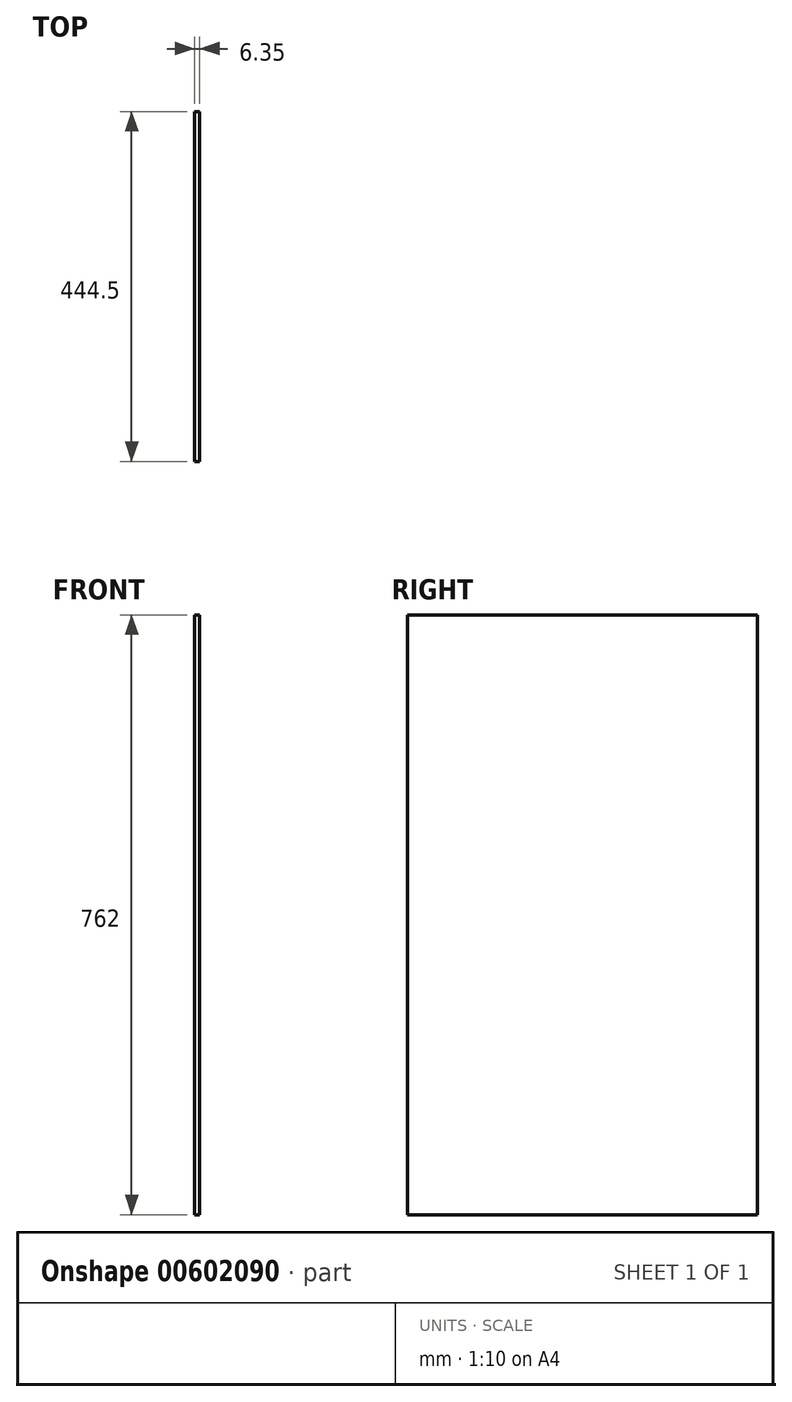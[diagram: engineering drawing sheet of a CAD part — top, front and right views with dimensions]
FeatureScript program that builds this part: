
annotation { "Feature Type Name" : "Feature", "Feature Type Description" : "" }
export const myFeature = defineFeature(function(context is Context, id is Id, definition is map)
    precondition{}
    {
        {
            var Q0;
            Q0=qCreatedBy(makeId("Right.planeOp"),FACE);
            var sketch = newSketch(context, id + "F0", { "sketchPlane" : qUnion([Q0])});
            skLineSegment(sketch, "E0.bottom", {"start": v(222.25, 381) * mm, "end": v(-222.25, 381) * mm});
            skLineSegment(sketch, "E0.top", {"start": v(222.25, -381) * mm, "end": v(-222.25, -381) * mm});
            skLineSegment(sketch, "E0.left", {"start": v(222.25, 381) * mm, "end": v(222.25, -381) * mm});
            skLineSegment(sketch, "E0.right", {"start": v(-222.25, 381) * mm, "end": v(-222.25, -381) * mm});
            skPoint(sketch, "E0.middle", {"position": v(0, 0) * mm});
            skSolve(sketch);
        }
        {
            var Q0;
            Q0=makeQuery(id+"F0.imprint","IMPRINT",FACE,{"disambiguationData":[TD([[makeQuery(id+"F0.imprint","IMPRINT",EDGE,{"derivedFrom":sQuery(id+"F0.wireOp",EDGE,"E0.bottom")}),1.0]])]});
            extrude(context, id + "F1", {"entities" : qUnion([Q0]), "depth" : 6.35 * mm, "offsetDistance" : 25.4 * mm});
        }
    });
